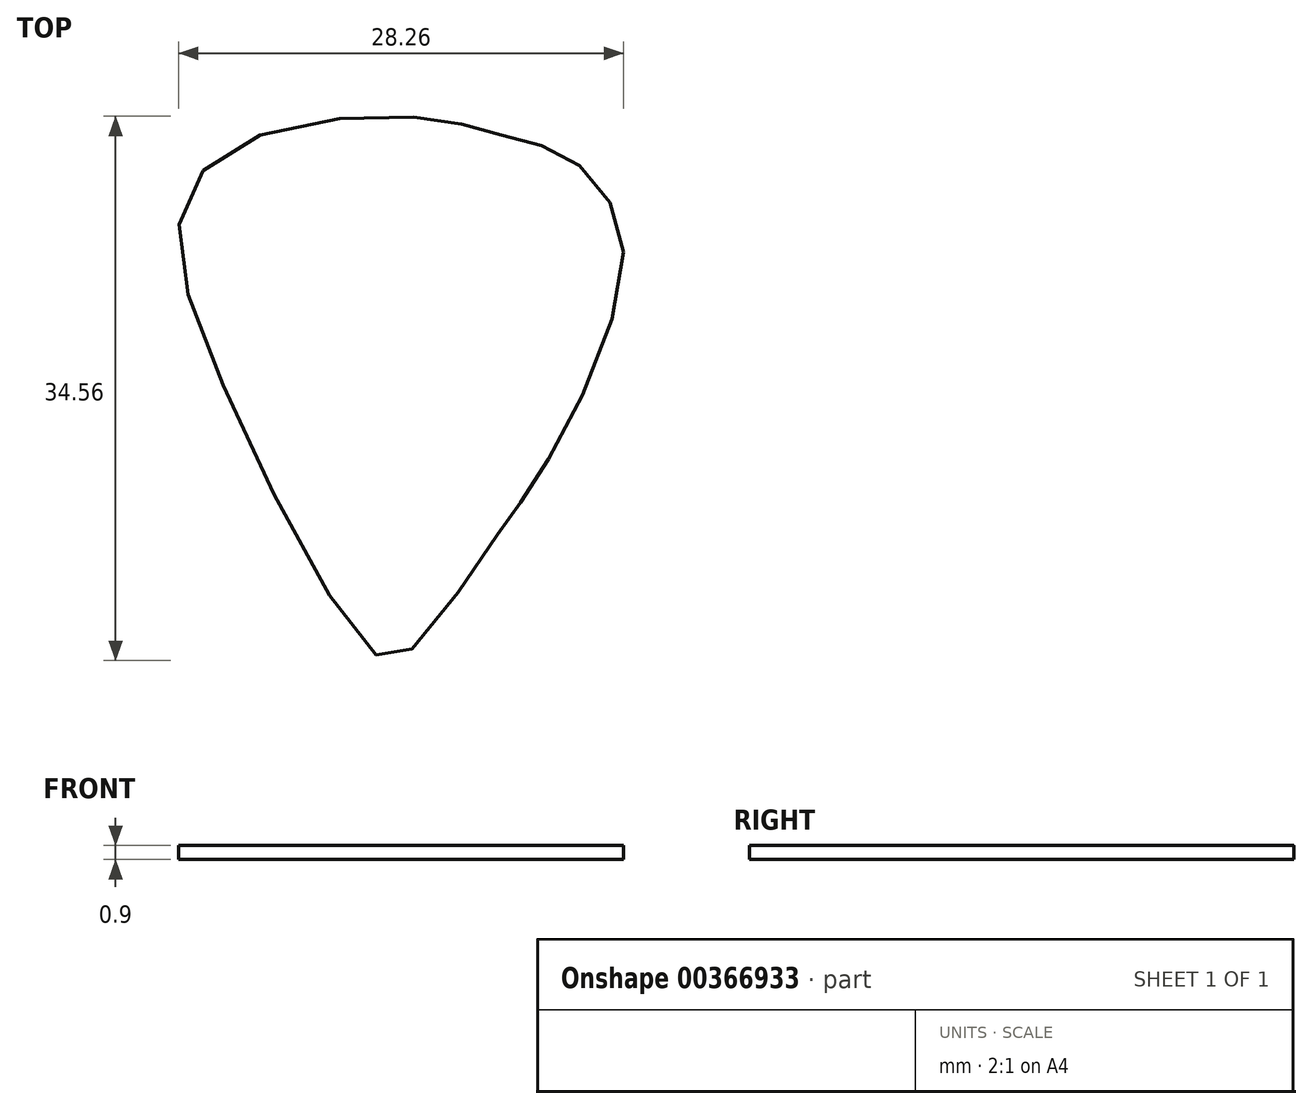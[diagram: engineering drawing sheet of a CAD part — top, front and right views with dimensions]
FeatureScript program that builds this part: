
annotation { "Feature Type Name" : "Feature", "Feature Type Description" : "" }
export const myFeature = defineFeature(function(context is Context, id is Id, definition is map)
    precondition{}
    {
        {
            var Q0;
            Q0=qCreatedBy(makeId("Top.planeOp"),FACE);
            var sketch = newSketch(context, id + "F0", { "sketchPlane" : qUnion([Q0])});
            skFitSpline(sketch, "E0", {"points": [v(-15.61, 0) * mm, v(-11.87, -0.63) * mm, v(-8.93, -1.45) * mm, v(-6.1, -2.4) * mm, v(-3.4, -5.05) * mm, v(-2.33, -9.64) * mm, v(-5.78, -19.42) * mm, v(-8.83, -24.49) * mm, v(-10.55, -26.9) * mm, v(-15.98, -34) * mm, v(-18.21, -34) * mm, v(-27.66, -17.21) * mm, v(-30.38, -6.04) * mm, v(-25.9, -1.36) * mm, v(-15.61, 0) * mm]});
            skSolve(sketch);
        }
        {
            var Q0;
            Q0 = qSketchRegion(id + "F0", true);
            extrude(context, id + "F1", {"entities" : qUnion([Q0]), "depth" : 0.9 * mm});
        }
    });
